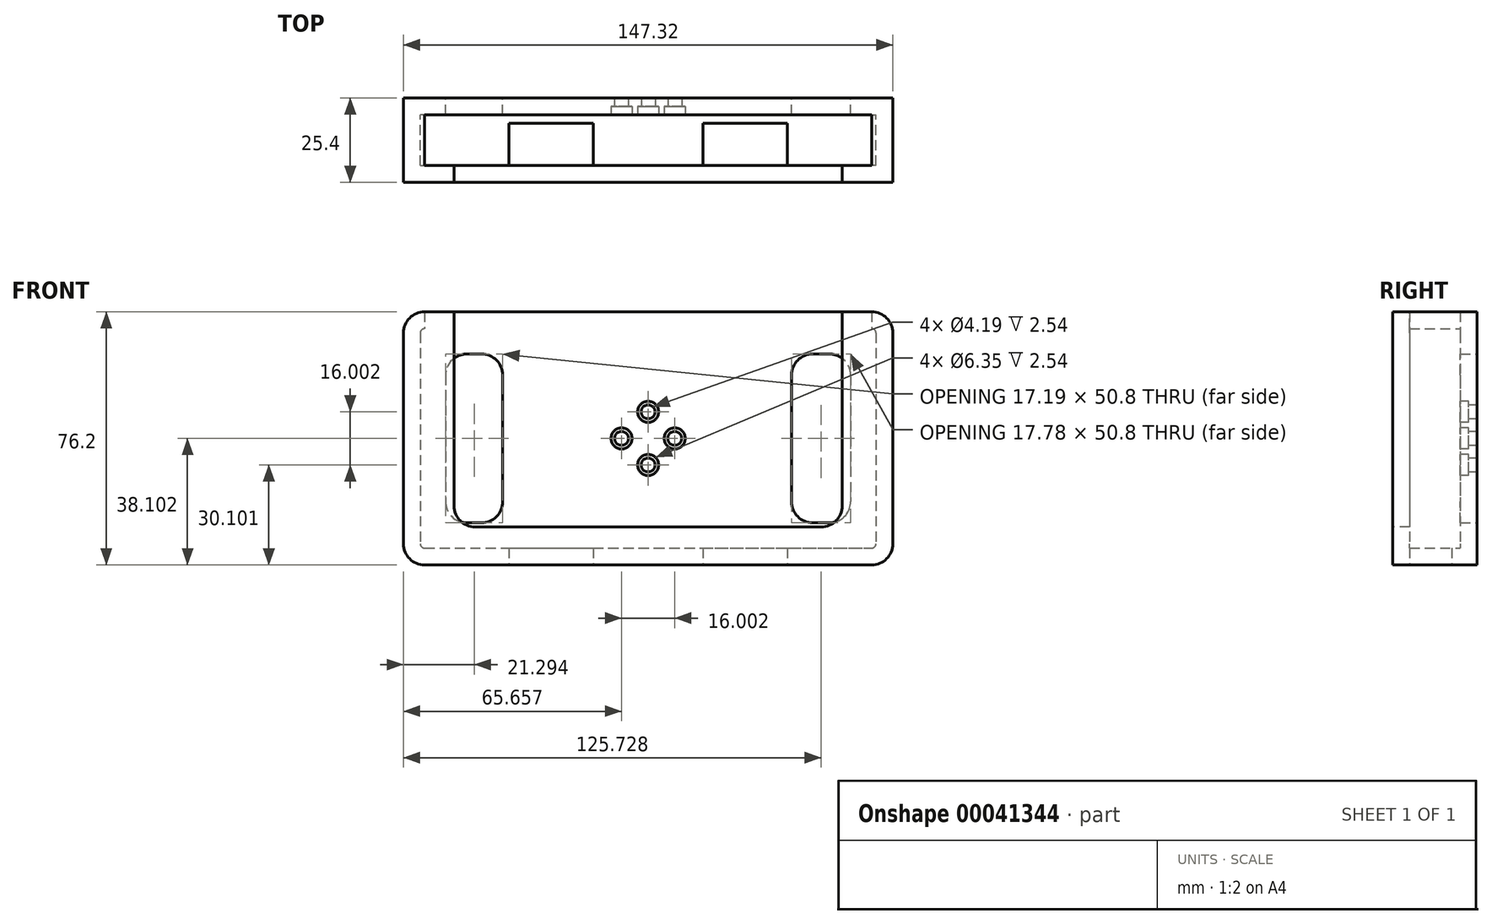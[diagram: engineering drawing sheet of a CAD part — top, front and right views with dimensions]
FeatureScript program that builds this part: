
annotation { "Feature Type Name" : "Feature", "Feature Type Description" : "" }
export const myFeature = defineFeature(function(context is Context, id is Id, definition is map)
    precondition{}
    {
        {
            var Q0;
            Q0=qCreatedBy(makeId("Front.planeOp"),FACE);
            var sketch = newSketch(context, id + "F0", { "sketchPlane" : qUnion([Q0])});
            skLineSegment(sketch, "E0.bottom", {"start": v(-90.71, 75.57) * mm, "end": v(43.9, 75.57) * mm});
            skLineSegment(sketch, "E0.top", {"start": v(-90.71, -0.63) * mm, "end": v(43.9, -0.63) * mm});
            skLineSegment(sketch, "E0.left", {"start": v(-97.06, 69.22) * mm, "end": v(-97.06, 5.72) * mm});
            skLineSegment(sketch, "E0.right", {"start": v(50.26, 69.22) * mm, "end": v(50.26, 5.72) * mm});
            skPoint(sketch, "E1.visualSharp", {"position": v(50.26, 75.57) * mm});
            skArc(sketch, "E1.filletArc", {"start": v(50.26, 69.22) * mm, "mid": v(48.4, 73.71) * mm, "end": v(43.9, 75.57) * mm});
            skPoint(sketch, "E2.visualSharp", {"position": v(-97.06, 75.57) * mm});
            skArc(sketch, "E2.filletArc", {"start": v(-90.71, 75.57) * mm, "mid": v(-95.2, 73.71) * mm, "end": v(-97.06, 69.22) * mm});
            skPoint(sketch, "E3.visualSharp", {"position": v(-97.06, -0.63) * mm});
            skArc(sketch, "E3.filletArc", {"start": v(-97.06, 5.72) * mm, "mid": v(-95.2, 1.23) * mm, "end": v(-90.71, -0.63) * mm});
            skPoint(sketch, "E4.visualSharp", {"position": v(50.26, -0.63) * mm});
            skArc(sketch, "E4.filletArc", {"start": v(43.9, -0.63) * mm, "mid": v(48.4, 1.23) * mm, "end": v(50.26, 5.72) * mm});
            skSolve(sketch);
        }
        {
            var Q0;
            Q0 = qSketchRegion(id + "F0", true);
            var Q1;
            Q1=makeQuery(id+"F0.imprint","IMPRINT",FACE,{"disambiguationData":[TD([[makeQuery(id+"F0.imprint","IMPRINT",EDGE,{"derivedFrom":sQuery(id+"F0.wireOp",EDGE,"E0.bottom")}),-1.0]])]});
            extrude(context, id + "F1", {"entities" : qUnion([Q0, Q1]), "depth" : 25.4 * mm});
        }
        {
            var Q0;
            Q0=makeQuery(id+"F1.opExtrude","SWEPT_FACE",FACE,{"disambiguationData":[OSD([sQuery(id+"F0.wireOp",EDGE,"E0.bottom")])]});
            shell(context, id + "F2", {"entities" : qUnion([Q0]), "thickness" : 5.08 * mm});
        }
        {
            var Q0;
            Q0=makeQuery(id+"F1.opExtrude","CAP_FACE",FACE,{"disambiguationData":[OSD([sQuery(id+"F0.wireOp",EDGE,"E0.bottom"),sQuery(id+"F0.wireOp",EDGE,"E0.top"),sQuery(id+"F0.wireOp",EDGE,"E0.left"),sQuery(id+"F0.wireOp",EDGE,"E0.right")])],"isStart":false});
            var sketch = newSketch(context, id + "F3", { "sketchPlane" : qUnion([Q0])});
            skLineSegment(sketch, "E5.bottom", {"start": v(-81.82, 75.57) * mm, "end": v(35.02, 75.57) * mm});
            skLineSegment(sketch, "E5.top", {"start": v(-75.47, 10.8) * mm, "end": v(28.67, 10.8) * mm});
            skLineSegment(sketch, "E5.left", {"start": v(-81.82, 75.57) * mm, "end": v(-81.82, 17.15) * mm});
            skLineSegment(sketch, "E5.right", {"start": v(35.02, 75.57) * mm, "end": v(35.02, 17.15) * mm});
            skPoint(sketch, "E6.visualSharp", {"position": v(-81.82, 10.8) * mm});
            skArc(sketch, "E6.filletArc", {"start": v(-81.82, 17.15) * mm, "mid": v(-79.96, 12.66) * mm, "end": v(-75.47, 10.8) * mm});
            skPoint(sketch, "E7.visualSharp", {"position": v(35.02, 10.8) * mm});
            skArc(sketch, "E7.filletArc", {"start": v(28.67, 10.8) * mm, "mid": v(33.16, 12.66) * mm, "end": v(35.02, 17.15) * mm});
            skSolve(sketch);
        }
        {
            var Q0;
            Q0=makeQuery(id+"F3.imprint","IMPRINT",FACE,{"disambiguationData":[TD([[makeQuery(id+"F3.imprint","IMPRINT",EDGE,{"derivedFrom":sQuery(id+"F3.wireOp",EDGE,"E5.bottom")}),-1.0]])]});
            extrude(context, id + "F4", {"entities" : qUnion([Q0]), "operationType" : NewBodyOperationType.REMOVE, "oppositeDirection" : true, "depth" : 5.08 * mm});
        }
        {
            var Q0;
            Q0=makeQuery(id+"F1.opExtrude","CAP_FACE",FACE,{"disambiguationData":[OSD([sQuery(id+"F0.wireOp",EDGE,"E0.bottom"),sQuery(id+"F0.wireOp",EDGE,"E0.top"),sQuery(id+"F0.wireOp",EDGE,"E0.left"),sQuery(id+"F0.wireOp",EDGE,"E0.right")])],"isStart":true});
            var sketch = newSketch(context, id + "F5", { "sketchPlane" : qUnion([Q0])});
            skLineSegment(sketch, "E8.bottom", {"start": v(-31.2, 62.87) * mm, "end": v(-26.13, 62.87) * mm});
            skLineSegment(sketch, "E8.top", {"start": v(-31.2, 12.07) * mm, "end": v(-26.13, 12.07) * mm});
            skLineSegment(sketch, "E8.left", {"start": v(-37.56, 56.52) * mm, "end": v(-37.56, 18.42) * mm});
            skLineSegment(sketch, "E8.right", {"start": v(-19.78, 56.52) * mm, "end": v(-19.78, 18.42) * mm});
            skPoint(sketch, "E9.visualSharp", {"position": v(-19.78, 62.87) * mm});
            skArc(sketch, "E9.filletArc", {"start": v(-19.78, 56.52) * mm, "mid": v(-21.64, 61.01) * mm, "end": v(-26.13, 62.87) * mm});
            skPoint(sketch, "E10.visualSharp", {"position": v(-37.56, 62.87) * mm});
            skArc(sketch, "E10.filletArc", {"start": v(-31.2, 62.87) * mm, "mid": v(-35.7, 61.01) * mm, "end": v(-37.56, 56.52) * mm});
            skPoint(sketch, "E11.visualSharp", {"position": v(-19.78, 12.07) * mm});
            skArc(sketch, "E11.filletArc", {"start": v(-26.13, 12.07) * mm, "mid": v(-21.64, 13.93) * mm, "end": v(-19.78, 18.42) * mm});
            skPoint(sketch, "E12.visualSharp", {"position": v(-37.56, 12.07) * mm});
            skArc(sketch, "E12.filletArc", {"start": v(-37.56, 18.42) * mm, "mid": v(-35.7, 13.93) * mm, "end": v(-31.2, 12.07) * mm});
            skLineSegment(sketch, "E13.bottom", {"start": v(73.52, 62.87) * mm, "end": v(78.01, 62.87) * mm});
            skLineSegment(sketch, "E13.top", {"start": v(73.52, 12.07) * mm, "end": v(78.01, 12.07) * mm});
            skLineSegment(sketch, "E13.left", {"start": v(67.17, 56.52) * mm, "end": v(67.17, 18.42) * mm});
            skLineSegment(sketch, "E13.right", {"start": v(84.36, 56.52) * mm, "end": v(84.36, 18.42) * mm});
            skPoint(sketch, "E14.visualSharp", {"position": v(84.36, 62.87) * mm});
            skArc(sketch, "E14.filletArc", {"start": v(84.36, 56.52) * mm, "mid": v(82.5, 61.01) * mm, "end": v(78.01, 62.87) * mm});
            skPoint(sketch, "E15.visualSharp", {"position": v(67.17, 62.87) * mm});
            skArc(sketch, "E15.filletArc", {"start": v(73.52, 62.87) * mm, "mid": v(69.03, 61.01) * mm, "end": v(67.17, 56.52) * mm});
            skPoint(sketch, "E16.visualSharp", {"position": v(84.36, 12.07) * mm});
            skArc(sketch, "E16.filletArc", {"start": v(78.01, 12.07) * mm, "mid": v(82.5, 13.93) * mm, "end": v(84.36, 18.42) * mm});
            skPoint(sketch, "E17.visualSharp", {"position": v(67.17, 12.07) * mm});
            skArc(sketch, "E17.filletArc", {"start": v(67.17, 18.42) * mm, "mid": v(69.03, 13.93) * mm, "end": v(73.52, 12.07) * mm});
            skSolve(sketch);
        }
        {
            var Q0;
            Q0=makeQuery(id+"F5.imprint","IMPRINT",FACE,{"disambiguationData":[TD([[makeQuery(id+"F5.imprint","IMPRINT",EDGE,{"derivedFrom":sQuery(id+"F5.wireOp",EDGE,"E8.bottom")}),-1.0]])]});
            var Q1;
            Q1=makeQuery(id+"F5.imprint","IMPRINT",FACE,{"disambiguationData":[TD([[makeQuery(id+"F5.imprint","IMPRINT",EDGE,{"derivedFrom":sQuery(id+"F5.wireOp",EDGE,"E13.bottom")}),-1.0]])]});
            extrude(context, id + "F6", {"entities" : qUnion([Q0, Q1]), "operationType" : NewBodyOperationType.REMOVE, "oppositeDirection" : true, "depth" : 5.08 * mm});
        }
        {
            var Q0;
            {var subQ0=sQuery(id+"F0.wireOp",EDGE,"E4.filletArc");var subQ1=sQuery(id+"F0.wireOp",EDGE,"E3.filletArc");var subQ2=sQuery(id+"F0.wireOp",EDGE,"E2.filletArc");var subQ3=sQuery(id+"F0.wireOp",EDGE,"E1.filletArc");var subQ4=sQuery(id+"F0.wireOp",EDGE,"E0.right");var subQ5=sQuery(id+"F0.wireOp",EDGE,"E0.left");var subQ6=sQuery(id+"F0.wireOp",EDGE,"E0.top");var subQ7=sQuery(id+"F0.wireOp",EDGE,"E0.bottom");Q0=makeQuery(id+"F2.opShell","OFFSET_FACE",FACE,{"disambiguationData":[OSD([subQ7,subQ6,subQ5,subQ4,subQ3,subQ2,subQ1,subQ0]),TDD([makeQuery(id+"F1.opExtrude","CAP_FACE",FACE,{"disambiguationData":[OSD([subQ7,subQ6,subQ5,subQ4,subQ3,subQ2,subQ1,subQ0])],"isStart":true})])]});}
            var sketch = newSketch(context, id + "F7", { "sketchPlane" : qUnion([Q0])});
            skPoint(sketch, "E18", {"position": v(-23.4, 37.47) * mm});
            skCircle(sketch, "E19", {"center": v(-23.4, 45.47) * mm, "radius": 2.1 * mm});
            skCircle(sketch, "E20", {"center": v(-15.4, 37.47) * mm, "radius": 2.1 * mm});
            skCircle(sketch, "E21", {"center": v(-23.4, 29.47) * mm, "radius": 2.1 * mm});
            skCircle(sketch, "E22", {"center": v(-31.4, 37.47) * mm, "radius": 2.1 * mm});
            skSolve(sketch);
        }
        {
            var Q0;
            Q0=makeQuery(id+"F7.imprint","IMPRINT",FACE,{"disambiguationData":[TD([[makeQuery(id+"F7.imprint","IMPRINT",EDGE,{"derivedFrom":sQuery(id+"F7.wireOp",EDGE,"E19")}),1.0]])]});
            var Q1;
            Q1=makeQuery(id+"F7.imprint","IMPRINT",FACE,{"disambiguationData":[TD([[makeQuery(id+"F7.imprint","IMPRINT",EDGE,{"derivedFrom":sQuery(id+"F7.wireOp",EDGE,"E22")}),1.0]])]});
            var Q2;
            Q2=makeQuery(id+"F7.imprint","IMPRINT",FACE,{"disambiguationData":[TD([[makeQuery(id+"F7.imprint","IMPRINT",EDGE,{"derivedFrom":sQuery(id+"F7.wireOp",EDGE,"E21")}),1.0]])]});
            var Q3;
            Q3=makeQuery(id+"F7.imprint","IMPRINT",FACE,{"disambiguationData":[TD([[makeQuery(id+"F7.imprint","IMPRINT",EDGE,{"derivedFrom":sQuery(id+"F7.wireOp",EDGE,"E20")}),1.0]])]});
            extrude(context, id + "F8", {"entities" : qUnion([Q0, Q1, Q2, Q3]), "operationType" : NewBodyOperationType.REMOVE, "oppositeDirection" : true, "depth" : 5.08 * mm});
        }
        {
            var Q0;
            {var subQ0=sQuery(id+"F0.wireOp",EDGE,"E4.filletArc");var subQ1=sQuery(id+"F0.wireOp",EDGE,"E3.filletArc");var subQ2=sQuery(id+"F0.wireOp",EDGE,"E2.filletArc");var subQ3=sQuery(id+"F0.wireOp",EDGE,"E1.filletArc");var subQ4=sQuery(id+"F0.wireOp",EDGE,"E0.right");var subQ5=sQuery(id+"F0.wireOp",EDGE,"E0.left");var subQ6=sQuery(id+"F0.wireOp",EDGE,"E0.top");var subQ7=sQuery(id+"F0.wireOp",EDGE,"E0.bottom");Q0=makeQuery(id+"F2.opShell","OFFSET_FACE",FACE,{"disambiguationData":[OSD([subQ7,subQ6,subQ5,subQ4,subQ3,subQ2,subQ1,subQ0]),TDD([makeQuery(id+"F1.opExtrude","CAP_FACE",FACE,{"disambiguationData":[OSD([subQ7,subQ6,subQ5,subQ4,subQ3,subQ2,subQ1,subQ0])],"isStart":true})])]});}
            var sketch = newSketch(context, id + "F9", { "sketchPlane" : qUnion([Q0])});
            skCircle(sketch, "E23", {"center": v(-23.4, 45.47) * mm, "radius": 3.18 * mm});
            skCircle(sketch, "E24", {"center": v(-15.4, 37.47) * mm, "radius": 3.18 * mm});
            skCircle(sketch, "E25", {"center": v(-23.4, 29.47) * mm, "radius": 3.18 * mm});
            skCircle(sketch, "E26", {"center": v(-31.4, 37.47) * mm, "radius": 3.18 * mm});
            skSolve(sketch);
        }
        {
            var Q0;
            Q0=makeQuery(id+"F9.imprint","IMPRINT",FACE,{"disambiguationData":[TD([[makeQuery(id+"F9.imprint","IMPRINT",EDGE,{"derivedFrom":sQuery(id+"F9.wireOp",EDGE,"E26")}),1.0]])]});
            var Q1;
            Q1=makeQuery(id+"F9.imprint","IMPRINT",FACE,{"disambiguationData":[TD([[makeQuery(id+"F9.imprint","IMPRINT",EDGE,{"derivedFrom":sQuery(id+"F9.wireOp",EDGE,"E23")}),1.0]])]});
            var Q2;
            Q2=makeQuery(id+"F9.imprint","IMPRINT",FACE,{"disambiguationData":[TD([[makeQuery(id+"F9.imprint","IMPRINT",EDGE,{"derivedFrom":sQuery(id+"F9.wireOp",EDGE,"E24")}),1.0]])]});
            var Q3;
            Q3=makeQuery(id+"F9.imprint","IMPRINT",FACE,{"disambiguationData":[TD([[makeQuery(id+"F9.imprint","IMPRINT",EDGE,{"derivedFrom":sQuery(id+"F9.wireOp",EDGE,"E25")}),1.0]])]});
            extrude(context, id + "F10", {"entities" : qUnion([Q0, Q1, Q2, Q3]), "operationType" : NewBodyOperationType.REMOVE, "oppositeDirection" : true, "depth" : 2.54 * mm});
        }
        {
            var Q0;
            Q0=makeQuery(id+"F1.opExtrude","SWEPT_FACE",FACE,{"disambiguationData":[OSD([sQuery(id+"F0.wireOp",EDGE,"E0.top")])]});
            var sketch = newSketch(context, id + "F11", { "sketchPlane" : qUnion([Q0])});
            skLineSegment(sketch, "E27.bottom", {"start": v(-65.31, 20.32) * mm, "end": v(-39.91, 20.32) * mm});
            skLineSegment(sketch, "E27.top", {"start": v(-65.31, 7.62) * mm, "end": v(-39.91, 7.62) * mm});
            skLineSegment(sketch, "E27.left", {"start": v(-65.31, 20.32) * mm, "end": v(-65.31, 7.62) * mm});
            skLineSegment(sketch, "E27.right", {"start": v(-39.91, 20.32) * mm, "end": v(-39.91, 7.62) * mm});
            skLineSegment(sketch, "E28.bottom", {"start": v(-6.9, 20.32) * mm, "end": v(18.5, 20.32) * mm});
            skLineSegment(sketch, "E28.top", {"start": v(-6.9, 7.62) * mm, "end": v(18.5, 7.62) * mm});
            skLineSegment(sketch, "E28.left", {"start": v(-6.9, 20.32) * mm, "end": v(-6.9, 7.62) * mm});
            skLineSegment(sketch, "E28.right", {"start": v(18.5, 20.32) * mm, "end": v(18.5, 7.62) * mm});
            skSolve(sketch);
        }
        {
            var Q0;
            Q0=makeQuery(id+"F11.imprint","IMPRINT",FACE,{"disambiguationData":[TD([[makeQuery(id+"F11.imprint","IMPRINT",EDGE,{"derivedFrom":sQuery(id+"F11.wireOp",EDGE,"E27.bottom")}),-1.0]])]});
            var Q1;
            Q1=makeQuery(id+"F11.imprint","IMPRINT",FACE,{"disambiguationData":[TD([[makeQuery(id+"F11.imprint","IMPRINT",EDGE,{"derivedFrom":sQuery(id+"F11.wireOp",EDGE,"E28.bottom")}),-1.0]])]});
            extrude(context, id + "F12", {"entities" : qUnion([Q0, Q1]), "operationType" : NewBodyOperationType.REMOVE, "oppositeDirection" : true, "depth" : 5.08 * mm});
        }
    });
